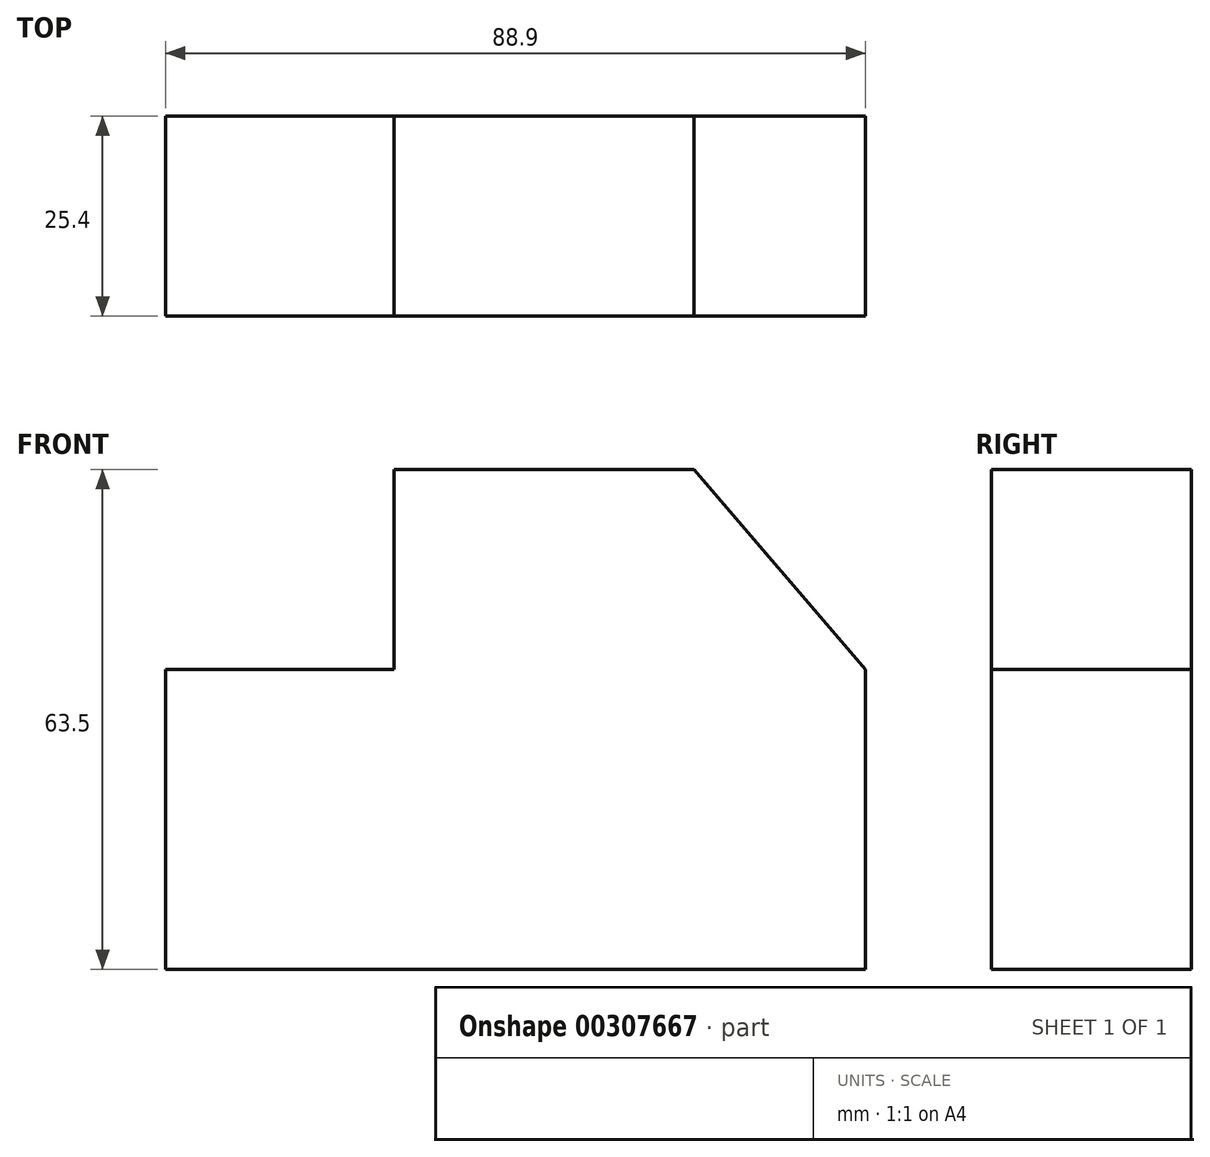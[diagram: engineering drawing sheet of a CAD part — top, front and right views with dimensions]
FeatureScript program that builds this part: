
annotation { "Feature Type Name" : "Feature", "Feature Type Description" : "" }
export const myFeature = defineFeature(function(context is Context, id is Id, definition is map)
    precondition{}
    {
        {
            var Q0;
            Q0=qCreatedBy(makeId("Front.planeOp"),FACE);
            var sketch = newSketch(context, id + "F0", { "sketchPlane" : qUnion([Q0])});
            skLineSegment(sketch, "E0", {"start": v(-37.64, -36.65) * mm, "end": v(51.26, -36.65) * mm});
            skLineSegment(sketch, "E1", {"start": v(51.26, -36.65) * mm, "end": v(51.26, 1.45) * mm});
            skLineSegment(sketch, "E2", {"start": v(51.26, 1.45) * mm, "end": v(29.48, 26.85) * mm});
            skLineSegment(sketch, "E3", {"start": v(29.48, 26.85) * mm, "end": v(-8.62, 26.85) * mm});
            skLineSegment(sketch, "E4", {"start": v(-8.62, 26.85) * mm, "end": v(-8.62, 1.45) * mm});
            skLineSegment(sketch, "E5", {"start": v(-8.62, 1.45) * mm, "end": v(-37.64, 1.45) * mm});
            skLineSegment(sketch, "E6", {"start": v(-37.64, 1.45) * mm, "end": v(-37.64, -36.65) * mm});
            skSolve(sketch);
        }
        {
            var Q0;
            Q0=makeQuery(id+"F0.imprint","IMPRINT",FACE,{"disambiguationData":[TD([[makeQuery(id+"F0.imprint","IMPRINT",EDGE,{"derivedFrom":sQuery(id+"F0.wireOp",EDGE,"E0")}),1.0]])]});
            extrude(context, id + "F1", {"entities" : qUnion([Q0]), "depth" : 25.4 * mm});
        }
    });
